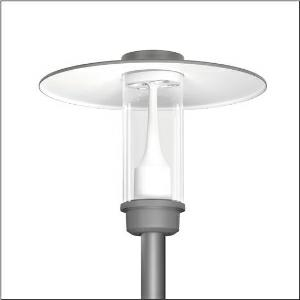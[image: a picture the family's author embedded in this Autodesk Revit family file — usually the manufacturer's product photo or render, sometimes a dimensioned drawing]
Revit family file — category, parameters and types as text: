
# Revit family: litepole_2_iq___p1_0a_5xa5425ff14h000022_e316
name_source: partatom
category: Lighting Fixtures
units: mm (PartAtom-declared; Revit-internal decimal feet)

## family parameters
Cut with Voids When Loaded = No
Host = Face
Light Source = No
Part Type = Normal
Room Calculation Point = No
Round Connector Dimension = Use Diameter
Shared = No

## types (1)
- --- (1 x LED, 1520 lm, 10.5 W, 3000K)
    Apparent Load = 11 VA
    CIE Flux Codes = 33 62 89 96 100
    Color Rendering = 70
    Color Temperature = 3000K
    Default Elevation = 1800 mm
    Description = Litepole 2 iQ, mast luminaire, Module 540 iQ-SR, primary light control with 3 zone facetted reflector, of plastic, silver coated, highly specular, structured, primary optical cover: cover, of PMMA, transparent, light distribution: P1.0a, light emission: direct distribution, primary light characteristic: strongly asymmetric, installation type: post-top, LED, High Power LED, rated luminous flux: 1.520lm, luminous efficacy: 145lm/W, light colour: 730, colour temperature: 3000K, control gear: iQ Street-Remote, control: Street-Remote, Auto-Match, Temp-Guard, Lumen-Switch, Night-Set, Smart-Wire, Light-Fading, Desk-Remote (wireless, voltage-free reading and setting of iQ features in the workshop via application-optimized NFC function/RFID function), optimised constant luminous flux control (CLO 2.0), pre-setting: logarithmic dimming characteristic, mains connection: 230..240V, AC, 50/60Hz, connection cable pre-assembled, cable length: 5,5m, wiring characteristics: H07RN-F, start of lifetime: 11W, end of service life: 11W, reduction: 5W, luminaire housing, upper part, of aluminium, coated, Siteco® metallic grey (DB 702S), diameter: 750mm, height: 590mm, spigot size: d x l = 76 x 70mm (post-top) | with reducer (optional accessory) 60 x 70mm, mounting height: 3..5m, post-top mast mounting element, of diecast aluminium, coated, Siteco® metallic grey (DB 702S), Module 540 iQ-SR, traffic white (RAL 9016), equipment: standard, protection rating (complete): IP65, insulation class (complete): insulation class II (safety insulation), certification: CE, ENEC, VDE, packaging unit: 1 piece

Light Distribution: P1.0a
    Height = 590 mm
    Lamp = 1 x LED
    Lamp Light Flux = 1520 lm
    Lamp Power = 10.5 W
    Lamp count = 1
    Length = 750 mm
    Luminous efficacy = 145 lm/W
    Manufacturer = Siteco
    ModVariant = No
    Model = 5XA5425FF14H000022
    Number of Poles = 1
    OnlyDefault = Yes
    Power Factor = 1
    Product Name = Litepole 2 iQ | P1.0a
    Product group = mast luminaire | pylon top
    ProductGroupID = 6100
    Protection Class = Protection class II
    Protection Degree = IP 65
    RLX_Detail_Level = 1
    RLX_Emergency_Light_Flux = 0 lm
    RLX_Emergency_Type = 0
    RLX_Emergency_Type_DB = No
    RlxData = <blob elided: 31141 chars, md5=ff161afd>
    Socket = socket
    Standby Power = 0 W
    System Light Flux = 1520 lm
    System Power = 11 W
    Type Comments = factory setting: luminous flux: 100 % | dim-lin: 254 | 419 mA
    Type Image = l_1006518.jpg
    URL = http://relux.com
    VarID = @adj_192448
    Voltage = 0 V
    Weight = 0.00 kg
    Width = 0 mm  [stored 0 ft]

note: [stored X ft] marks values corroborated as IEEE doubles in the binary element streams (Revit-internal decimal feet)

## geometry (parser evidence)
native form markers: Blend x4, Sweep x9
no freeform markers — native parametric forms only
